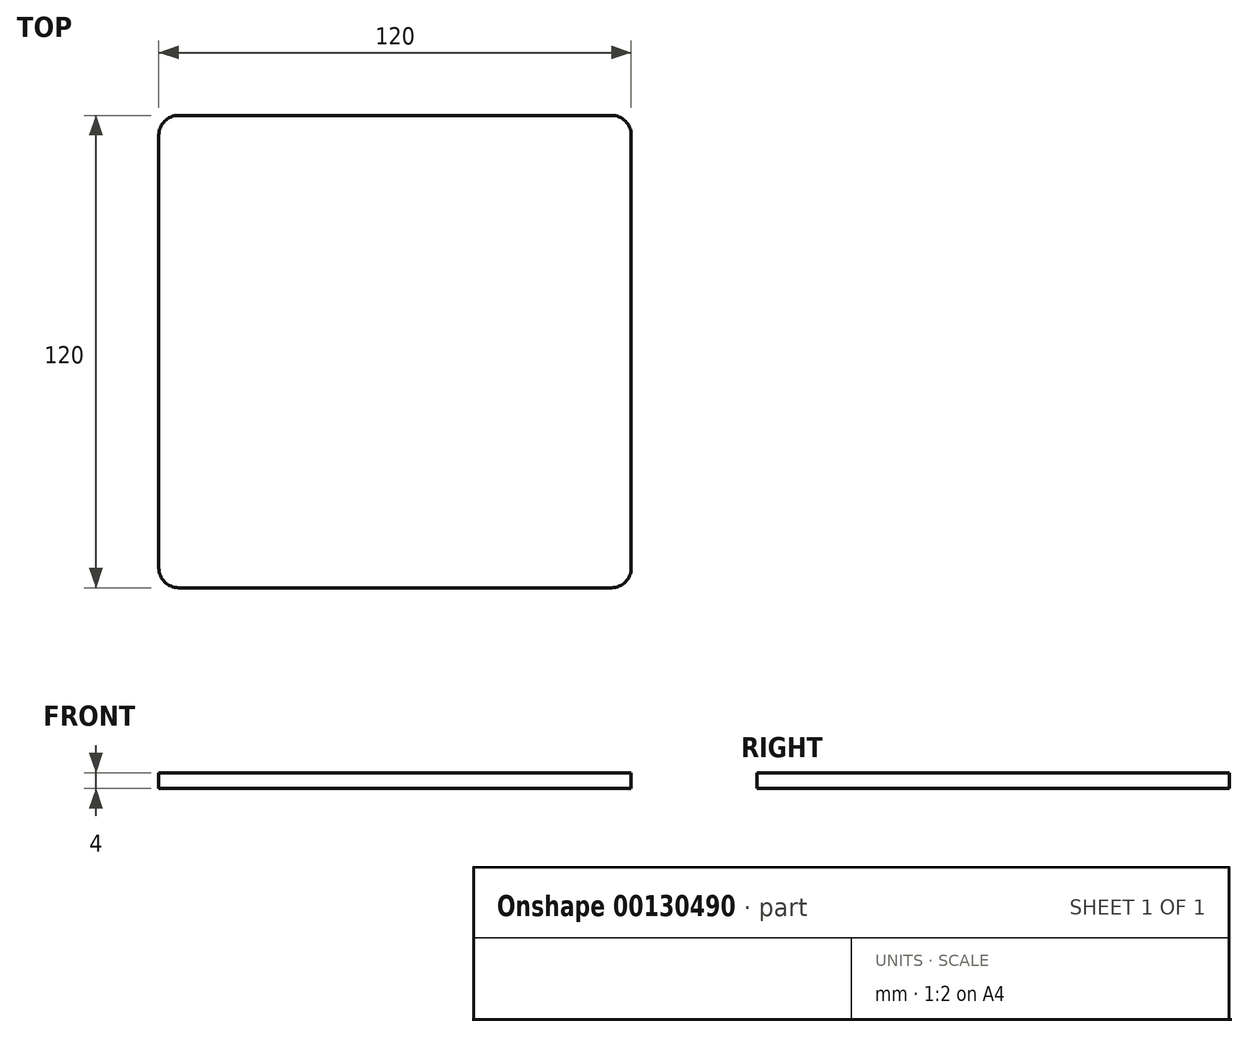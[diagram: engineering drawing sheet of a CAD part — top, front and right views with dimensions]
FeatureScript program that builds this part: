
annotation { "Feature Type Name" : "Feature", "Feature Type Description" : "" }
export const myFeature = defineFeature(function(context is Context, id is Id, definition is map)
    precondition{}
    {
        {
            var Q0;
            Q0=qCreatedBy(makeId("Top.planeOp"),FACE);
            var sketch = newSketch(context, id + "F0", { "sketchPlane" : qUnion([Q0])});
            skLineSegment(sketch, "E0.bottom", {"start": v(60, -60) * mm, "end": v(-60, -60) * mm});
            skLineSegment(sketch, "E0.top", {"start": v(60, 60) * mm, "end": v(-60, 60) * mm});
            skLineSegment(sketch, "E0.left", {"start": v(60, -60) * mm, "end": v(60, 60) * mm});
            skLineSegment(sketch, "E0.right", {"start": v(-60, -60) * mm, "end": v(-60, 60) * mm});
            skPoint(sketch, "E0.middle", {"position": v(0, 0) * mm});
            skSolve(sketch);
        }
        {
            var Q0;
            Q0=makeQuery(id+"F0.imprint","IMPRINT",FACE,{"disambiguationData":[TD([[makeQuery(id+"F0.imprint","IMPRINT",EDGE,{"derivedFrom":sQuery(id+"F0.wireOp",EDGE,"E0.bottom")}),-1.0]])]});
            var Q1;
            Q1 = qSketchRegion(id + "F0", true);
            extrude(context, id + "F1", {"entities" : qUnion([Q0, Q1]), "depth" : 4 * mm});
        }
        {
            var Q0;
            Q0=makeQuery(id+"F1.opExtrude","SWEPT_EDGE",EDGE,{"disambiguationData":[OSD([sQuery(id+"F0.wireOp",EDGE,"E0.bottom"),sQuery(id+"F0.wireOp",EDGE,"E0.left")])]});
            var Q1;
            Q1=makeQuery(id+"F1.opExtrude","SWEPT_EDGE",EDGE,{"disambiguationData":[OSD([sQuery(id+"F0.wireOp",EDGE,"E0.bottom"),sQuery(id+"F0.wireOp",EDGE,"E0.right")])]});
            var Q2;
            Q2=makeQuery(id+"F1.opExtrude","SWEPT_EDGE",EDGE,{"disambiguationData":[OSD([sQuery(id+"F0.wireOp",EDGE,"E0.top"),sQuery(id+"F0.wireOp",EDGE,"E0.left")])]});
            var Q3;
            Q3=makeQuery(id+"F1.opExtrude","SWEPT_EDGE",EDGE,{"disambiguationData":[OSD([sQuery(id+"F0.wireOp",EDGE,"E0.top"),sQuery(id+"F0.wireOp",EDGE,"E0.right")])]});
            fillet(context, id + "F2", {"entities" : qUnion([Q0, Q1, Q2, Q3]), "radius" : 5 * mm, "tangentPropagation" : true, "allowEdgeOverflow" : false});
        }
    });
